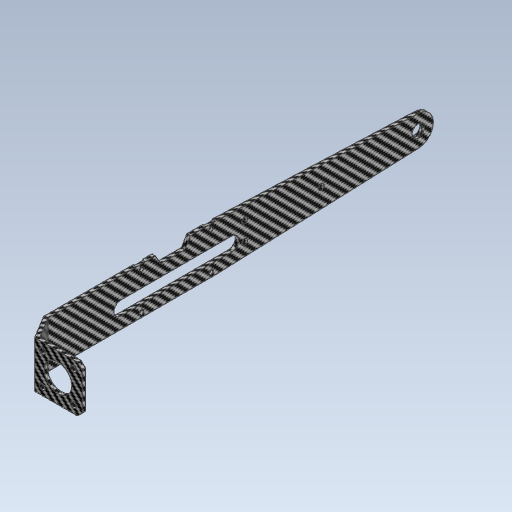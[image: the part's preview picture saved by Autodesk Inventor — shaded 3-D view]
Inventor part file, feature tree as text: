
AUTODESK INVENTOR PART (.ipt)
format: ipt  version: 2024 (Build 280153000, 153)  size: 228,864 bytes
history: native  units: mm
features: other x4, chamfer x2, sketch x2, extrude x1
ambient origin geometry x8: Origin, YZ Plane, XZ Plane, XY Plane, X Axis, Y Axis, Z Axis, Center Point
bodies: Body1 (feature_tree)
feature tree (9):
  other  "_bridseye_sketch.ipt"
  chamfer  "面取り1"  Distance=10.0mm
  chamfer  "面取り2"  Distance=0.5mm Angle=45.0deg
  sketch  "スケッチ1"
  sketch  "スケッチ3"
  extrude  "押し出し1"  Depth=2.0mm TaperAngle=45.0deg
  other  "ソリッド27::_bridseye_sketch.ipt"
  other  "TaggingFeature2"
  other  "side_links-link2"
